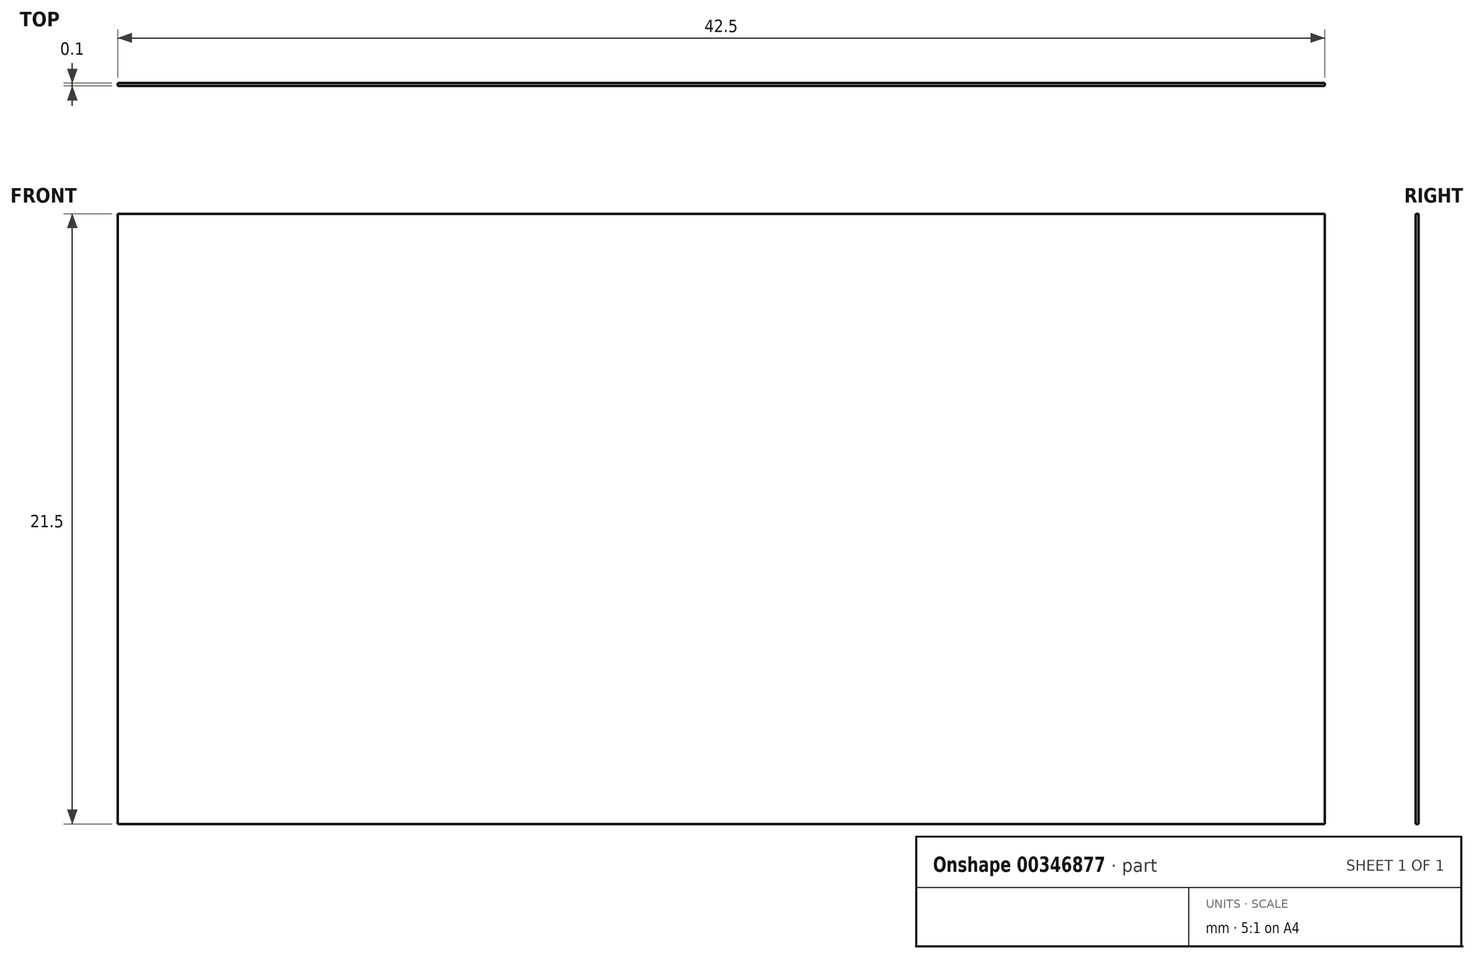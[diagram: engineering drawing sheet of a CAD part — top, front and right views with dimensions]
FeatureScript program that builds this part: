
annotation { "Feature Type Name" : "Feature", "Feature Type Description" : "" }
export const myFeature = defineFeature(function(context is Context, id is Id, definition is map)
    precondition{}
    {
        {
            var Q0;
            Q0=qCreatedBy(makeId("Front.planeOp"),FACE);
            var sketch = newSketch(context, id + "F0", { "sketchPlane" : qUnion([Q0])});
            skLineSegment(sketch, "E0.bottom", {"start": v(21.25, 10.75) * mm, "end": v(-21.25, 10.75) * mm});
            skLineSegment(sketch, "E0.top", {"start": v(21.25, -10.75) * mm, "end": v(-21.25, -10.75) * mm});
            skLineSegment(sketch, "E0.left", {"start": v(21.25, 10.75) * mm, "end": v(21.25, -10.75) * mm});
            skLineSegment(sketch, "E0.right", {"start": v(-21.25, 10.75) * mm, "end": v(-21.25, -10.75) * mm});
            skPoint(sketch, "E0.middle", {"position": v(0, 0) * mm});
            skSolve(sketch);
        }
        {
            var Q0;
            Q0=makeQuery(id+"F0.imprint","IMPRINT",FACE,{"disambiguationData":[TD([[makeQuery(id+"F0.imprint","IMPRINT",EDGE,{"derivedFrom":sQuery(id+"F0.wireOp",EDGE,"E0.bottom")}),1.0]])]});
            extrude(context, id + "F1", {"entities" : qUnion([Q0]), "depth" : 0.1 * mm});
        }
    });
